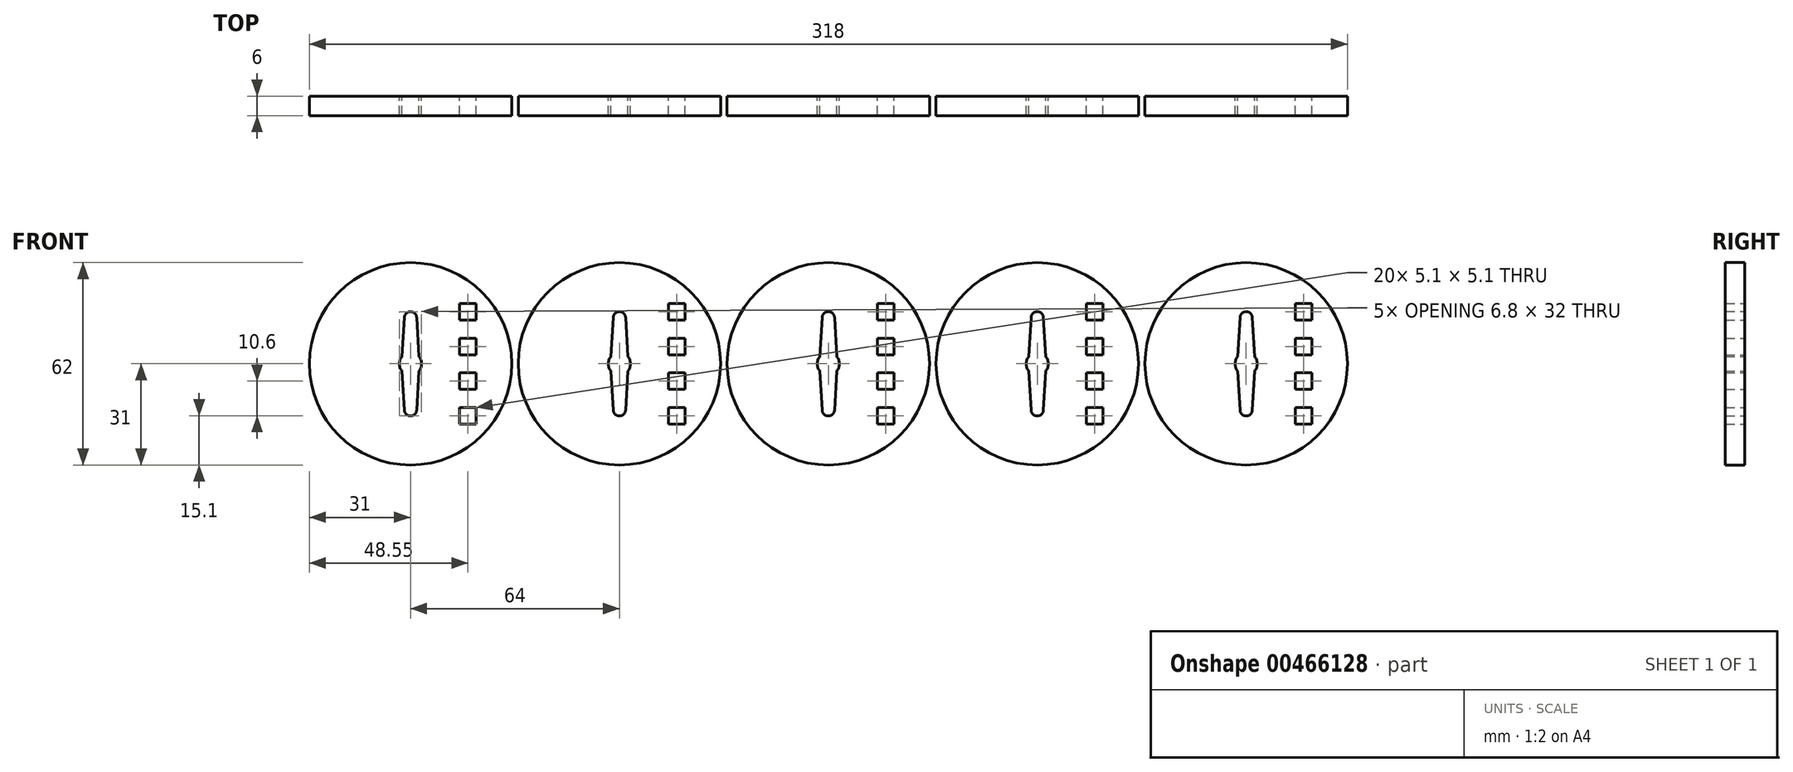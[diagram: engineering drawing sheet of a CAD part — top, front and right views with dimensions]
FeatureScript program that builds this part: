
annotation { "Feature Type Name" : "Feature", "Feature Type Description" : "" }
export const myFeature = defineFeature(function(context is Context, id is Id, definition is map)
    precondition{}
    {
        {
            var Q0;
            Q0=qCreatedBy(makeId("Front.planeOp"),FACE);
            var sketch = newSketch(context, id + "F0", { "sketchPlane" : qUnion([Q0])});
            skCircle(sketch, "E0", {"center": v(0, 0) * mm, "radius": 31 * mm});
            skLineSegment(sketch, "E1.bottom", {"start": v(15, 18.45) * mm, "end": v(20.1, 18.45) * mm});
            skLineSegment(sketch, "E1.top", {"start": v(15, 13.35) * mm, "end": v(20.1, 13.35) * mm});
            skLineSegment(sketch, "E1.left", {"start": v(15, 18.45) * mm, "end": v(15, 13.35) * mm});
            skLineSegment(sketch, "E1.right", {"start": v(20.1, 18.45) * mm, "end": v(20.1, 13.35) * mm});
            skLineSegment(sketch, "E2.bottom", {"start": v(15, 7.85) * mm, "end": v(20.1, 7.85) * mm});
            skLineSegment(sketch, "E2.top", {"start": v(15, 2.75) * mm, "end": v(20.1, 2.75) * mm});
            skLineSegment(sketch, "E2.left", {"start": v(15, 7.85) * mm, "end": v(15, 2.75) * mm});
            skLineSegment(sketch, "E2.right", {"start": v(20.1, 7.85) * mm, "end": v(20.1, 2.75) * mm});
            skLineSegment(sketch, "E3.bottom", {"start": v(15, -2.75) * mm, "end": v(20.1, -2.75) * mm});
            skLineSegment(sketch, "E3.top", {"start": v(15, -7.85) * mm, "end": v(20.1, -7.85) * mm});
            skLineSegment(sketch, "E3.left", {"start": v(15, -2.75) * mm, "end": v(15, -7.85) * mm});
            skLineSegment(sketch, "E3.right", {"start": v(20.1, -2.75) * mm, "end": v(20.1, -7.85) * mm});
            skLineSegment(sketch, "E4.bottom", {"start": v(15, -13.35) * mm, "end": v(20.1, -13.35) * mm});
            skLineSegment(sketch, "E4.top", {"start": v(15, -18.45) * mm, "end": v(20.1, -18.45) * mm});
            skLineSegment(sketch, "E4.left", {"start": v(15, -13.35) * mm, "end": v(15, -18.45) * mm});
            skLineSegment(sketch, "E4.right", {"start": v(20.1, -13.35) * mm, "end": v(20.1, -18.45) * mm});
            skCircle(sketch, "E5", {"center": v(0, 0) * mm, "radius": 3.4 * mm, "construction": true});
            skCircle(sketch, "E6", {"center": v(0, 14.1) * mm, "radius": 1.9 * mm, "construction": true});
            skCircle(sketch, "E7", {"center": v(0, -14.1) * mm, "radius": 1.9 * mm, "construction": true});
            skLineSegment(sketch, "E8", {"start": v(-1.9, 14.21) * mm, "end": v(-2.6, 2.2) * mm});
            skLineSegment(sketch, "E9", {"start": v(2.6, 2.2) * mm, "end": v(1.9, 14.21) * mm});
            skLineSegment(sketch, "E10", {"start": v(-1.9, -14.21) * mm, "end": v(-2.6, -2.2) * mm});
            skLineSegment(sketch, "E11", {"start": v(2.6, -2.2) * mm, "end": v(1.9, -14.21) * mm});
            skArc(sketch, "E12", {"start": v(-1.9, 14.21) * mm, "mid": v(0, 16) * mm, "end": v(1.9, 14.21) * mm});
            skArc(sketch, "E13", {"start": v(1.9, -14.21) * mm, "mid": v(0, -16) * mm, "end": v(-1.9, -14.21) * mm});
            skPoint(sketch, "E14", {"position": v(0, 16) * mm});
            skPoint(sketch, "E15", {"position": v(0, -16) * mm});
            skArc(sketch, "E16", {"start": v(-2.6, -2.2) * mm, "mid": v(-3.4, 0) * mm, "end": v(-2.6, 2.2) * mm});
            skArc(sketch, "E17", {"start": v(2.6, 2.2) * mm, "mid": v(3.4, 0) * mm, "end": v(2.6, -2.2) * mm});
            skLineSegment(sketch, "E18.1.0.0", {"start": v(79, -13.35) * mm, "end": v(84.1, -13.35) * mm});
            skLineSegment(sketch, "E18.1.0.1", {"start": v(84.1, -2.75) * mm, "end": v(84.1, -7.85) * mm});
            skLineSegment(sketch, "E18.1.0.2", {"start": v(79, 18.45) * mm, "end": v(84.1, 18.45) * mm});
            skLineSegment(sketch, "E18.1.0.3", {"start": v(66.6, 2.2) * mm, "end": v(65.9, 14.21) * mm});
            skLineSegment(sketch, "E18.1.0.4", {"start": v(84.1, 18.45) * mm, "end": v(84.1, 13.35) * mm});
            skLineSegment(sketch, "E18.1.0.5", {"start": v(79, 7.85) * mm, "end": v(84.1, 7.85) * mm});
            skCircle(sketch, "E18.1.0.6", {"center": v(64, -14.1) * mm, "radius": 1.9 * mm, "construction": true});
            skLineSegment(sketch, "E18.1.0.7", {"start": v(79, -13.35) * mm, "end": v(79, -18.45) * mm});
            skLineSegment(sketch, "E18.1.0.8", {"start": v(84.1, 7.85) * mm, "end": v(84.1, 2.75) * mm});
            skCircle(sketch, "E18.1.0.9", {"center": v(64, 0) * mm, "radius": 31 * mm});
            skLineSegment(sketch, "E18.1.0.10", {"start": v(79, -2.75) * mm, "end": v(84.1, -2.75) * mm});
            skPoint(sketch, "E18.1.0.11", {"position": v(64, -16) * mm});
            skLineSegment(sketch, "E18.1.0.12", {"start": v(79, 18.45) * mm, "end": v(79, 13.35) * mm});
            skLineSegment(sketch, "E18.1.0.13", {"start": v(79, 7.85) * mm, "end": v(79, 2.75) * mm});
            skLineSegment(sketch, "E18.1.0.14", {"start": v(84.1, -13.35) * mm, "end": v(84.1, -18.45) * mm});
            skLineSegment(sketch, "E18.1.0.15", {"start": v(79, -7.85) * mm, "end": v(84.1, -7.85) * mm});
            skCircle(sketch, "E18.1.0.16", {"center": v(64, 14.1) * mm, "radius": 1.9 * mm, "construction": true});
            skLineSegment(sketch, "E18.1.0.17", {"start": v(79, 13.35) * mm, "end": v(84.1, 13.35) * mm});
            skLineSegment(sketch, "E18.1.0.18", {"start": v(66.6, -2.2) * mm, "end": v(65.9, -14.21) * mm});
            skCircle(sketch, "E18.1.0.19", {"center": v(64, 0) * mm, "radius": 3.4 * mm, "construction": true});
            skLineSegment(sketch, "E18.1.0.20", {"start": v(62.1, 14.21) * mm, "end": v(61.4, 2.2) * mm});
            skLineSegment(sketch, "E18.1.0.21", {"start": v(79, -2.75) * mm, "end": v(79, -7.85) * mm});
            skLineSegment(sketch, "E18.1.0.22", {"start": v(79, -18.45) * mm, "end": v(84.1, -18.45) * mm});
            skLineSegment(sketch, "E18.1.0.23", {"start": v(62.1, -14.21) * mm, "end": v(61.4, -2.2) * mm});
            skLineSegment(sketch, "E18.1.0.24", {"start": v(79, 2.75) * mm, "end": v(84.1, 2.75) * mm});
            skPoint(sketch, "E18.1.0.25", {"position": v(64, 16) * mm});
            skArc(sketch, "E18.1.0.26", {"start": v(65.9, -14.21) * mm, "mid": v(64, -16) * mm, "end": v(62.1, -14.21) * mm});
            skArc(sketch, "E18.1.0.27", {"start": v(62.1, 14.21) * mm, "mid": v(64, 16) * mm, "end": v(65.9, 14.21) * mm});
            skArc(sketch, "E18.1.0.28", {"start": v(61.4, -2.2) * mm, "mid": v(60.6, 0) * mm, "end": v(61.4, 2.2) * mm});
            skArc(sketch, "E18.1.0.29", {"start": v(66.6, 2.2) * mm, "mid": v(67.4, 0) * mm, "end": v(66.6, -2.2) * mm});
            skLineSegment(sketch, "E18.2.0.0", {"start": v(143, -13.35) * mm, "end": v(148.1, -13.35) * mm});
            skLineSegment(sketch, "E18.2.0.1", {"start": v(148.1, -2.75) * mm, "end": v(148.1, -7.85) * mm});
            skLineSegment(sketch, "E18.2.0.2", {"start": v(143, 18.45) * mm, "end": v(148.1, 18.45) * mm});
            skLineSegment(sketch, "E18.2.0.3", {"start": v(130.6, 2.2) * mm, "end": v(129.9, 14.21) * mm});
            skLineSegment(sketch, "E18.2.0.4", {"start": v(148.1, 18.45) * mm, "end": v(148.1, 13.35) * mm});
            skLineSegment(sketch, "E18.2.0.5", {"start": v(143, 7.85) * mm, "end": v(148.1, 7.85) * mm});
            skCircle(sketch, "E18.2.0.6", {"center": v(128, -14.1) * mm, "radius": 1.9 * mm, "construction": true});
            skLineSegment(sketch, "E18.2.0.7", {"start": v(143, -13.35) * mm, "end": v(143, -18.45) * mm});
            skLineSegment(sketch, "E18.2.0.8", {"start": v(148.1, 7.85) * mm, "end": v(148.1, 2.75) * mm});
            skCircle(sketch, "E18.2.0.9", {"center": v(128, 0) * mm, "radius": 31 * mm});
            skLineSegment(sketch, "E18.2.0.10", {"start": v(143, -2.75) * mm, "end": v(148.1, -2.75) * mm});
            skPoint(sketch, "E18.2.0.11", {"position": v(128, -16) * mm});
            skLineSegment(sketch, "E18.2.0.12", {"start": v(143, 18.45) * mm, "end": v(143, 13.35) * mm});
            skLineSegment(sketch, "E18.2.0.13", {"start": v(143, 7.85) * mm, "end": v(143, 2.75) * mm});
            skLineSegment(sketch, "E18.2.0.14", {"start": v(148.1, -13.35) * mm, "end": v(148.1, -18.45) * mm});
            skLineSegment(sketch, "E18.2.0.15", {"start": v(143, -7.85) * mm, "end": v(148.1, -7.85) * mm});
            skCircle(sketch, "E18.2.0.16", {"center": v(128, 14.1) * mm, "radius": 1.9 * mm, "construction": true});
            skLineSegment(sketch, "E18.2.0.17", {"start": v(143, 13.35) * mm, "end": v(148.1, 13.35) * mm});
            skLineSegment(sketch, "E18.2.0.18", {"start": v(130.6, -2.2) * mm, "end": v(129.9, -14.21) * mm});
            skCircle(sketch, "E18.2.0.19", {"center": v(128, 0) * mm, "radius": 3.4 * mm, "construction": true});
            skLineSegment(sketch, "E18.2.0.20", {"start": v(126.1, 14.21) * mm, "end": v(125.4, 2.2) * mm});
            skLineSegment(sketch, "E18.2.0.21", {"start": v(143, -2.75) * mm, "end": v(143, -7.85) * mm});
            skLineSegment(sketch, "E18.2.0.22", {"start": v(143, -18.45) * mm, "end": v(148.1, -18.45) * mm});
            skLineSegment(sketch, "E18.2.0.23", {"start": v(126.1, -14.21) * mm, "end": v(125.4, -2.2) * mm});
            skLineSegment(sketch, "E18.2.0.24", {"start": v(143, 2.75) * mm, "end": v(148.1, 2.75) * mm});
            skPoint(sketch, "E18.2.0.25", {"position": v(128, 16) * mm});
            skArc(sketch, "E18.2.0.26", {"start": v(129.9, -14.21) * mm, "mid": v(128, -16) * mm, "end": v(126.1, -14.21) * mm});
            skArc(sketch, "E18.2.0.27", {"start": v(126.1, 14.21) * mm, "mid": v(128, 16) * mm, "end": v(129.9, 14.21) * mm});
            skArc(sketch, "E18.2.0.28", {"start": v(125.4, -2.2) * mm, "mid": v(124.6, 0) * mm, "end": v(125.4, 2.2) * mm});
            skArc(sketch, "E18.2.0.29", {"start": v(130.6, 2.2) * mm, "mid": v(131.4, 0) * mm, "end": v(130.6, -2.2) * mm});
            skLineSegment(sketch, "E18.direction1", {"start": v(-1.9, -14.21) * mm, "end": v(62.1, -14.21) * mm, "construction": true});
            skLineSegment(sketch, "E19.0.3.0", {"start": v(207, -13.35) * mm, "end": v(212.1, -13.35) * mm});
            skLineSegment(sketch, "E19.3.3.0", {"start": v(212.1, -2.75) * mm, "end": v(212.1, -7.85) * mm});
            skLineSegment(sketch, "E19.6.3.0", {"start": v(207, 18.45) * mm, "end": v(212.1, 18.45) * mm});
            skLineSegment(sketch, "E19.9.3.0", {"start": v(194.6, 2.2) * mm, "end": v(193.9, 14.21) * mm});
            skLineSegment(sketch, "E19.12.3.0", {"start": v(212.1, 18.45) * mm, "end": v(212.1, 13.35) * mm});
            skLineSegment(sketch, "E19.15.3.0", {"start": v(207, 7.85) * mm, "end": v(212.1, 7.85) * mm});
            skCircle(sketch, "E19.18.3.0", {"center": v(192, -14.1) * mm, "radius": 1.9 * mm, "construction": true});
            skLineSegment(sketch, "E19.20.3.0", {"start": v(207, -13.35) * mm, "end": v(207, -18.45) * mm});
            skLineSegment(sketch, "E19.23.3.0", {"start": v(212.1, 7.85) * mm, "end": v(212.1, 2.75) * mm});
            skCircle(sketch, "E19.26.3.0", {"center": v(192, 0) * mm, "radius": 31 * mm});
            skLineSegment(sketch, "E19.28.3.0", {"start": v(207, -2.75) * mm, "end": v(212.1, -2.75) * mm});
            skPoint(sketch, "E19.31.3.0", {"position": v(192, -16) * mm});
            skLineSegment(sketch, "E19.32.3.0", {"start": v(207, 18.45) * mm, "end": v(207, 13.35) * mm});
            skLineSegment(sketch, "E19.35.3.0", {"start": v(207, 7.85) * mm, "end": v(207, 2.75) * mm});
            skLineSegment(sketch, "E19.38.3.0", {"start": v(212.1, -13.35) * mm, "end": v(212.1, -18.45) * mm});
            skLineSegment(sketch, "E19.41.3.0", {"start": v(207, -7.85) * mm, "end": v(212.1, -7.85) * mm});
            skCircle(sketch, "E19.44.3.0", {"center": v(192, 14.1) * mm, "radius": 1.9 * mm, "construction": true});
            skLineSegment(sketch, "E19.46.3.0", {"start": v(207, 13.35) * mm, "end": v(212.1, 13.35) * mm});
            skLineSegment(sketch, "E19.49.3.0", {"start": v(194.6, -2.2) * mm, "end": v(193.9, -14.21) * mm});
            skCircle(sketch, "E19.52.3.0", {"center": v(192, 0) * mm, "radius": 3.4 * mm, "construction": true});
            skLineSegment(sketch, "E19.54.3.0", {"start": v(190.1, 14.21) * mm, "end": v(189.4, 2.2) * mm});
            skLineSegment(sketch, "E19.57.3.0", {"start": v(207, -2.75) * mm, "end": v(207, -7.85) * mm});
            skLineSegment(sketch, "E19.60.3.0", {"start": v(207, -18.45) * mm, "end": v(212.1, -18.45) * mm});
            skLineSegment(sketch, "E19.63.3.0", {"start": v(190.1, -14.21) * mm, "end": v(189.4, -2.2) * mm});
            skLineSegment(sketch, "E19.66.3.0", {"start": v(207, 2.75) * mm, "end": v(212.1, 2.75) * mm});
            skPoint(sketch, "E19.69.3.0", {"position": v(192, 16) * mm});
            skArc(sketch, "E19.70.3.0", {"start": v(193.9, -14.21) * mm, "mid": v(192, -16) * mm, "end": v(190.1, -14.21) * mm});
            skArc(sketch, "E19.74.3.0", {"start": v(190.1, 14.21) * mm, "mid": v(192, 16) * mm, "end": v(193.9, 14.21) * mm});
            skArc(sketch, "E19.78.3.0", {"start": v(189.4, -2.2) * mm, "mid": v(188.6, 0) * mm, "end": v(189.4, 2.2) * mm});
            skArc(sketch, "E19.82.3.0", {"start": v(194.6, 2.2) * mm, "mid": v(195.4, 0) * mm, "end": v(194.6, -2.2) * mm});
            skLineSegment(sketch, "E19.0.4.0", {"start": v(271, -13.35) * mm, "end": v(276.1, -13.35) * mm});
            skLineSegment(sketch, "E19.3.4.0", {"start": v(276.1, -2.75) * mm, "end": v(276.1, -7.85) * mm});
            skLineSegment(sketch, "E19.6.4.0", {"start": v(271, 18.45) * mm, "end": v(276.1, 18.45) * mm});
            skLineSegment(sketch, "E19.9.4.0", {"start": v(258.6, 2.2) * mm, "end": v(257.9, 14.21) * mm});
            skLineSegment(sketch, "E19.12.4.0", {"start": v(276.1, 18.45) * mm, "end": v(276.1, 13.35) * mm});
            skLineSegment(sketch, "E19.15.4.0", {"start": v(271, 7.85) * mm, "end": v(276.1, 7.85) * mm});
            skCircle(sketch, "E19.18.4.0", {"center": v(256, -14.1) * mm, "radius": 1.9 * mm, "construction": true});
            skLineSegment(sketch, "E19.20.4.0", {"start": v(271, -13.35) * mm, "end": v(271, -18.45) * mm});
            skLineSegment(sketch, "E19.23.4.0", {"start": v(276.1, 7.85) * mm, "end": v(276.1, 2.75) * mm});
            skCircle(sketch, "E19.26.4.0", {"center": v(256, 0) * mm, "radius": 31 * mm});
            skLineSegment(sketch, "E19.28.4.0", {"start": v(271, -2.75) * mm, "end": v(276.1, -2.75) * mm});
            skPoint(sketch, "E19.31.4.0", {"position": v(256, -16) * mm});
            skLineSegment(sketch, "E19.32.4.0", {"start": v(271, 18.45) * mm, "end": v(271, 13.35) * mm});
            skLineSegment(sketch, "E19.35.4.0", {"start": v(271, 7.85) * mm, "end": v(271, 2.75) * mm});
            skLineSegment(sketch, "E19.38.4.0", {"start": v(276.1, -13.35) * mm, "end": v(276.1, -18.45) * mm});
            skLineSegment(sketch, "E19.41.4.0", {"start": v(271, -7.85) * mm, "end": v(276.1, -7.85) * mm});
            skCircle(sketch, "E19.44.4.0", {"center": v(256, 14.1) * mm, "radius": 1.9 * mm, "construction": true});
            skLineSegment(sketch, "E19.46.4.0", {"start": v(271, 13.35) * mm, "end": v(276.1, 13.35) * mm});
            skLineSegment(sketch, "E19.49.4.0", {"start": v(258.6, -2.2) * mm, "end": v(257.9, -14.21) * mm});
            skCircle(sketch, "E19.52.4.0", {"center": v(256, 0) * mm, "radius": 3.4 * mm, "construction": true});
            skLineSegment(sketch, "E19.54.4.0", {"start": v(254.1, 14.21) * mm, "end": v(253.4, 2.2) * mm});
            skLineSegment(sketch, "E19.57.4.0", {"start": v(271, -2.75) * mm, "end": v(271, -7.85) * mm});
            skLineSegment(sketch, "E19.60.4.0", {"start": v(271, -18.45) * mm, "end": v(276.1, -18.45) * mm});
            skLineSegment(sketch, "E19.63.4.0", {"start": v(254.1, -14.21) * mm, "end": v(253.4, -2.2) * mm});
            skLineSegment(sketch, "E19.66.4.0", {"start": v(271, 2.75) * mm, "end": v(276.1, 2.75) * mm});
            skPoint(sketch, "E19.69.4.0", {"position": v(256, 16) * mm});
            skArc(sketch, "E19.70.4.0", {"start": v(257.9, -14.21) * mm, "mid": v(256, -16) * mm, "end": v(254.1, -14.21) * mm});
            skArc(sketch, "E19.74.4.0", {"start": v(254.1, 14.21) * mm, "mid": v(256, 16) * mm, "end": v(257.9, 14.21) * mm});
            skArc(sketch, "E19.78.4.0", {"start": v(253.4, -2.2) * mm, "mid": v(252.6, 0) * mm, "end": v(253.4, 2.2) * mm});
            skArc(sketch, "E19.82.4.0", {"start": v(258.6, 2.2) * mm, "mid": v(259.4, 0) * mm, "end": v(258.6, -2.2) * mm});
            skSolve(sketch);
        }
        {
            var Q0;
            Q0=qSketchRegion(id+"F0",true);
            extrude(context, id + "F1", {"entities" : qUnion([Q0]), "depth" : 6 * mm});
        }
    });
